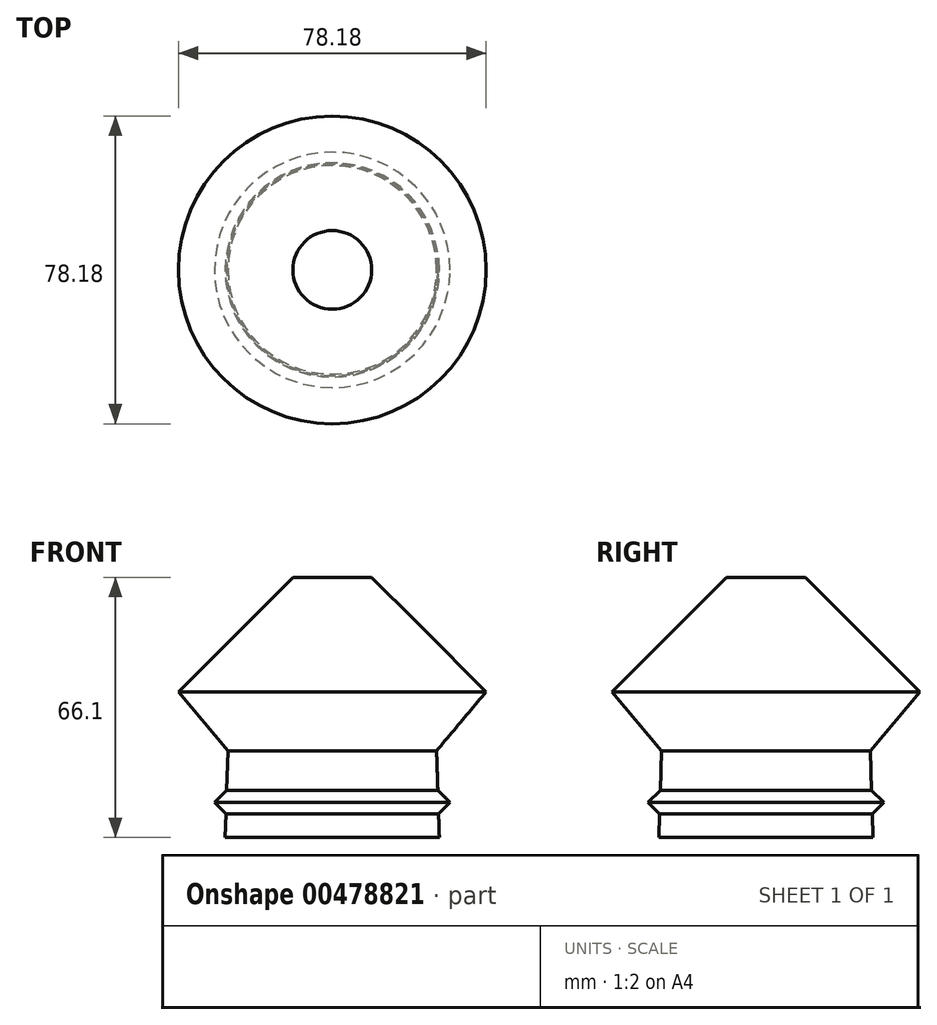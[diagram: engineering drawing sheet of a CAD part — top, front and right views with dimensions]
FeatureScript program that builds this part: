
annotation { "Feature Type Name" : "Feature", "Feature Type Description" : "" }
export const myFeature = defineFeature(function(context is Context, id is Id, definition is map)
    precondition{}
    {
        {
            var Q0;
            Q0=qCreatedBy(makeId("Front.planeOp"),FACE);
            var sketch = newSketch(context, id + "F0", { "sketchPlane" : qUnion([Q0])});
            skLineSegment(sketch, "E0", {"start": v(0, 0) * mm, "end": v(27.2, 0) * mm});
            skLineSegment(sketch, "E1", {"start": v(27.2, 0) * mm, "end": v(27, 6) * mm});
            skPoint(sketch, "E2", {"position": v(39.09, 37) * mm});
            skPoint(sketch, "E3", {"position": v(10, 66.1) * mm});
            skLineSegment(sketch, "E4", {"start": v(26.5, 22) * mm, "end": v(39.09, 37) * mm});
            skLineSegment(sketch, "E5", {"start": v(10, 66.1) * mm, "end": v(22.42, 53.67) * mm});
            skLineSegment(sketch, "E6", {"start": v(10, 66.1) * mm, "end": v(0, 66.1) * mm});
            skLineSegment(sketch, "E7", {"start": v(0, 66.1) * mm, "end": v(0, 0) * mm});
            skLineSegment(sketch, "E8", {"start": v(39.09, 37) * mm, "end": v(18.96, 37) * mm, "construction": true});
            skLineSegment(sketch, "E9", {"start": v(10, 66.1) * mm, "end": v(31.85, 66.1) * mm, "construction": true});
            skLineSegment(sketch, "E10", {"start": v(27, 6) * mm, "end": v(29.92, 8.9) * mm});
            skLineSegment(sketch, "E11", {"start": v(29.92, 8.9) * mm, "end": v(26.82, 12) * mm});
            skLineSegment(sketch, "E12", {"start": v(29.92, 8.9) * mm, "end": v(12.74, 8.9) * mm, "construction": true});
            skLineSegment(sketch, "E13", {"start": v(27, 6) * mm, "end": v(26.82, 12) * mm, "construction": true});
            skLineSegment(sketch, "E14", {"start": v(26.82, 12) * mm, "end": v(26.5, 22) * mm});
            skLineSegment(sketch, "E15", {"start": v(24.54, 51.55) * mm, "end": v(26.66, 53.67) * mm, "construction": true});
            skLineSegment(sketch, "E16", {"start": v(26.66, 53.67) * mm, "end": v(26.66, 49.43) * mm});
            skLineSegment(sketch, "E17", {"start": v(26.66, 53.67) * mm, "end": v(22.42, 53.67) * mm});
            skLineSegment(sketch, "E18", {"start": v(26.66, 49.43) * mm, "end": v(39.09, 37) * mm});
            skLineSegment(sketch, "E19", {"start": v(22.42, 53.67) * mm, "end": v(26.66, 49.43) * mm});
            skSolve(sketch);
        }
        {
            var Q0;
            Q0=makeQuery(id+"F0.imprint","IMPRINT",FACE,{"disambiguationData":[TD([[makeQuery(id+"F0.imprint","IMPRINT",EDGE,{"derivedFrom":sQuery(id+"F0.wireOp",EDGE,"E0")}),1.0]])]});
            var Q1;
            Q1=sQuery(id+"F0.wireOp",EDGE,"E7");
            revolve(context, id + "F1", {"entities" : qUnion([Q0]), "axis" : qUnion([Q1]), "revolveType" : RevolveType.FULL});
        }
    });
